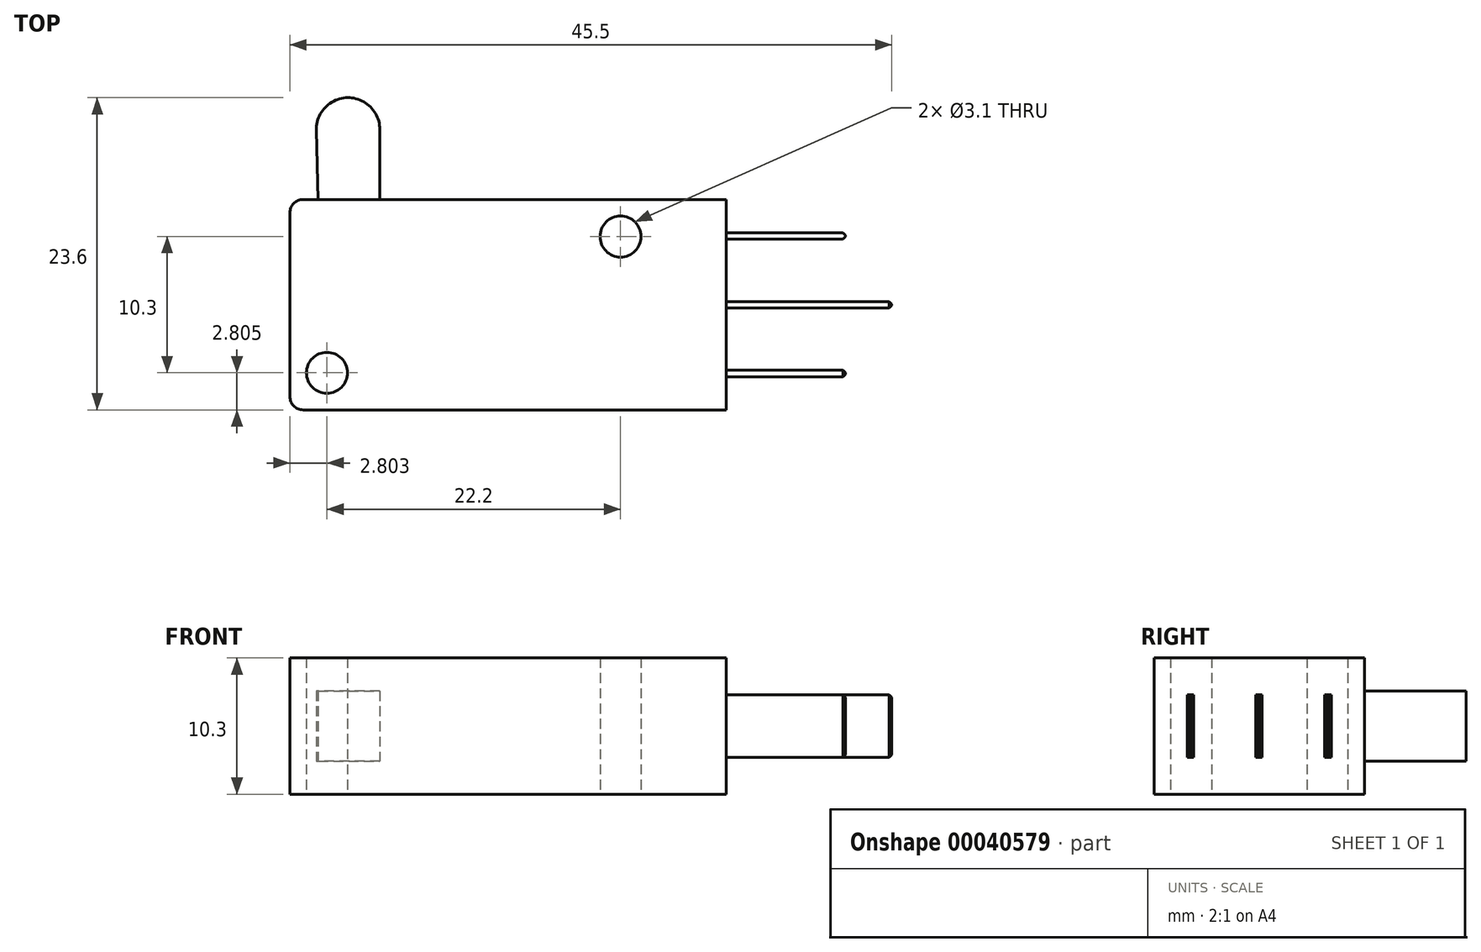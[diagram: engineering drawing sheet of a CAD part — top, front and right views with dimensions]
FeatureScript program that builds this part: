
annotation { "Feature Type Name" : "Feature", "Feature Type Description" : "" }
export const myFeature = defineFeature(function(context is Context, id is Id, definition is map)
    precondition{}
    {
        {
            var Q0;
            Q0=qCreatedBy(makeId("Top.planeOp"),FACE);
            var sketch = newSketch(context, id + "F0", { "sketchPlane" : qUnion([Q0])});
            skLineSegment(sketch, "E0.bottom", {"start": v(-25.87, -19.74) * mm, "end": v(7.13, -19.74) * mm});
            skLineSegment(sketch, "E0.top", {"start": v(-25.87, -35.64) * mm, "end": v(7.13, -35.64) * mm});
            skLineSegment(sketch, "E0.left", {"start": v(-25.87, -19.74) * mm, "end": v(-25.87, -35.64) * mm});
            skLineSegment(sketch, "E0.right", {"start": v(7.13, -19.74) * mm, "end": v(7.13, -35.64) * mm});
            skPoint(sketch, "E1", {"position": v(-23.07, -32.84) * mm});
            skPoint(sketch, "E2", {"position": v(-0.87, -22.54) * mm});
            skCircle(sketch, "E3", {"center": v(-21.47, -14.44) * mm, "radius": 2.4 * mm});
            skLineSegment(sketch, "E4", {"start": v(-19.07, -14.44) * mm, "end": v(-19.07, -19.74) * mm});
            skLineSegment(sketch, "E5", {"start": v(-23.87, -14.5) * mm, "end": v(-23.73, -19.74) * mm});
            skCircle(sketch, "E6", {"center": v(-0.87, -22.54) * mm, "radius": 1.55 * mm});
            skCircle(sketch, "E7", {"center": v(-23.07, -32.84) * mm, "radius": 1.55 * mm});
            skSolve(sketch);
        }
        {
            var Q0;
            Q0=makeQuery(id+"F0.imprint","IMPRINT",FACE,{"disambiguationData":[TD([[makeQuery(id+"F0.imprint","IMPRINT",EDGE,{"derivedFrom":sQuery(id+"F0.wireOp",EDGE,"E0.top")}),1.0]])]});
            var Q1;
            {var subQ0=sQuery(id+"F0.wireOp",EDGE,"E4");Q1=makeQuery(id+"F0.imprint","IMPRINT",FACE,{"disambiguationData":[TD([[makeQuery(id+"F0.imprint","IMPRINT",EDGE,{"derivedFrom":subQ0}),-1.0]])]});}
            var Q2;
            {var subQ0=sQuery(id+"F0.wireOp",EDGE,"E3");var subQ1=makeQuery(id+"F0.imprint","INTERSECT",VERTEX,{"derivedFrom":[subQ0,sQuery(id+"F0.wireOp",EDGE,"E4")]});Q2=makeQuery(id+"F0.imprint","IMPRINT",FACE,{"disambiguationData":[TD([[makeQuery(id+"F0.imprint","IMPRINT",EDGE,{"disambiguationData":[TD([[subQ1,-1.0]])],"derivedFrom":subQ0}),1.0]])]});}
            extrude(context, id + "F1", {"entities" : qUnion([Q0, Q1, Q2]), "depth" : 10.3 * mm});
        }
        {
            var Q0;
            Q0=makeQuery(id+"F1.opExtrude","CAP_FACE",FACE,{"disambiguationData":[OSD([sQuery(id+"F0.wireOp",EDGE,"E0.bottom"),sQuery(id+"F0.wireOp",EDGE,"E0.top"),sQuery(id+"F0.wireOp",EDGE,"E0.left"),sQuery(id+"F0.wireOp",EDGE,"E0.right"),sQuery(id+"F0.wireOp",EDGE,"E3"),sQuery(id+"F0.wireOp",EDGE,"E4"),sQuery(id+"F0.wireOp",EDGE,"E5"),sQuery(id+"F0.wireOp",EDGE,"E6"),sQuery(id+"F0.wireOp",EDGE,"E7")])],"isStart":false});
            var sketch = newSketch(context, id + "F2", { "sketchPlane" : qUnion([Q0])});
            skLineSegment(sketch, "E8", {"start": v(-23.73, -19.74) * mm, "end": v(-19.07, -19.74) * mm});
            skSolve(sketch);
        }
        {
            var Q0;
            Q0=makeQuery(id+"F2.imprint","IMPRINT",FACE,{"disambiguationData":[TD([[makeQuery(id+"F2.imprint","IMPRINT",EDGE,{"derivedFrom":sQuery(id+"F2.wireOp",EDGE,"E8")}),1.0]])]});
            extrude(context, id + "F3", {"entities" : qUnion([Q0]), "operationType" : NewBodyOperationType.REMOVE, "oppositeDirection" : true, "depth" : 2.5 * mm});
        }
        {
            var Q0;
            {var subQ0=sQuery(id+"F0.wireOp",EDGE,"E4");Q0=makeQuery(id+"F0.imprint","IMPRINT",FACE,{"disambiguationData":[TD([[makeQuery(id+"F0.imprint","IMPRINT",EDGE,{"derivedFrom":subQ0}),-1.0]])]});}
            var Q1;
            {var subQ0=sQuery(id+"F0.wireOp",EDGE,"E3");var subQ1=makeQuery(id+"F0.imprint","INTERSECT",VERTEX,{"derivedFrom":[subQ0,sQuery(id+"F0.wireOp",EDGE,"E4")]});Q1=makeQuery(id+"F0.imprint","IMPRINT",FACE,{"disambiguationData":[TD([[makeQuery(id+"F0.imprint","IMPRINT",EDGE,{"disambiguationData":[TD([[subQ1,-1.0]])],"derivedFrom":subQ0}),1.0]])]});}
            extrude(context, id + "F4", {"entities" : qUnion([Q0, Q1]), "operationType" : NewBodyOperationType.REMOVE, "depth" : 2.5 * mm});
        }
        {
            var Q0;
            Q0=makeQuery(id+"F1.opExtrude","SWEPT_FACE",FACE,{"disambiguationData":[OSD([sQuery(id+"F0.wireOp",EDGE,"E0.right")])]});
            var sketch = newSketch(context, id + "F5", { "sketchPlane" : qUnion([Q0])});
            skLineSegment(sketch, "E9", {"start": v(-22.24, 10.3) * mm, "end": v(-22.24, 0) * mm, "construction": true});
            skLineSegment(sketch, "E10", {"start": v(-22.74, 10.3) * mm, "end": v(-22.74, 0) * mm, "construction": true});
            skLineSegment(sketch, "E11", {"start": v(-27.44, 10.3) * mm, "end": v(-27.44, 0) * mm, "construction": true});
            skLineSegment(sketch, "E12", {"start": v(-27.94, 10.3) * mm, "end": v(-27.94, 0) * mm, "construction": true});
            skLineSegment(sketch, "E13", {"start": v(-32.64, 10.3) * mm, "end": v(-32.64, 0) * mm, "construction": true});
            skLineSegment(sketch, "E14", {"start": v(-33.14, 10.3) * mm, "end": v(-33.14, 0) * mm, "construction": true});
            skLineSegment(sketch, "E15", {"start": v(-19.74, 5.15) * mm, "end": v(-35.64, 5.15) * mm, "construction": true});
            skLineSegment(sketch, "E16", {"start": v(-19.74, 7.53) * mm, "end": v(-35.64, 7.53) * mm, "construction": true});
            skLineSegment(sketch, "E17.MirrorCS", {"start": v(-19.74, 2.78) * mm, "end": v(-35.64, 2.78) * mm, "construction": true});
            skPoint(sketch, "E18.oppositeSnap0", {"position": v(-22.74, 5.15) * mm});
            skLineSegment(sketch, "E18.bottom", {"start": v(-22.24, 7.53) * mm, "end": v(-22.74, 7.53) * mm});
            skLineSegment(sketch, "E18.top", {"start": v(-22.24, 2.78) * mm, "end": v(-22.74, 2.78) * mm});
            skLineSegment(sketch, "E18.left", {"start": v(-22.24, 7.53) * mm, "end": v(-22.24, 2.78) * mm});
            skLineSegment(sketch, "E18.right", {"start": v(-22.74, 7.53) * mm, "end": v(-22.74, 2.78) * mm});
            skPoint(sketch, "E19.oppositeSnap0", {"position": v(-27.94, 5.15) * mm});
            skLineSegment(sketch, "E19.bottom", {"start": v(-27.46, 7.53) * mm, "end": v(-27.94, 7.53) * mm});
            skLineSegment(sketch, "E19.top", {"start": v(-27.46, 2.78) * mm, "end": v(-27.94, 2.78) * mm});
            skLineSegment(sketch, "E19.left", {"start": v(-27.46, 7.53) * mm, "end": v(-27.46, 2.78) * mm});
            skLineSegment(sketch, "E19.right", {"start": v(-27.94, 7.53) * mm, "end": v(-27.94, 2.78) * mm});
            skLineSegment(sketch, "E20.bottom", {"start": v(-32.64, 7.53) * mm, "end": v(-33.14, 7.53) * mm});
            skLineSegment(sketch, "E20.top", {"start": v(-32.64, 2.78) * mm, "end": v(-33.14, 2.78) * mm});
            skLineSegment(sketch, "E20.left", {"start": v(-32.64, 7.53) * mm, "end": v(-32.64, 2.78) * mm});
            skLineSegment(sketch, "E20.right", {"start": v(-33.14, 7.53) * mm, "end": v(-33.14, 2.78) * mm});
            skSolve(sketch);
        }
        {
            var Q0;
            Q0=makeQuery(id+"F5.imprint","IMPRINT",FACE,{"disambiguationData":[TD([[makeQuery(id+"F5.imprint","IMPRINT",EDGE,{"derivedFrom":sQuery(id+"F5.wireOp",EDGE,"E18.bottom")}),1.0]])]});
            var Q1;
            Q1=makeQuery(id+"F5.imprint","IMPRINT",FACE,{"disambiguationData":[TD([[makeQuery(id+"F5.imprint","IMPRINT",EDGE,{"derivedFrom":sQuery(id+"F5.wireOp",EDGE,"E20.bottom")}),1.0]])]});
            extrude(context, id + "F6", {"entities" : qUnion([Q0, Q1]), "operationType" : NewBodyOperationType.ADD, "depth" : 9 * mm});
        }
        {
            var Q0;
            Q0=makeQuery(id+"F5.imprint","IMPRINT",FACE,{"disambiguationData":[TD([[makeQuery(id+"F5.imprint","IMPRINT",EDGE,{"derivedFrom":sQuery(id+"F5.wireOp",EDGE,"E19.bottom")}),1.0]])]});
            extrude(context, id + "F7", {"entities" : qUnion([Q0]), "operationType" : NewBodyOperationType.ADD, "depth" : 12.5 * mm});
        }
        {
            var Q0;
            Q0=makeQuery(id+"F6.opExtrude","CAP_EDGE",EDGE,{"disambiguationData":[OSD([sQuery(id+"F5.wireOp",EDGE,"E18.left")])],"isStart":false});
            var Q1;
            Q1=makeQuery(id+"F6.opExtrude","CAP_EDGE",EDGE,{"disambiguationData":[OSD([sQuery(id+"F5.wireOp",EDGE,"E18.right")])],"isStart":false});
            var Q2;
            Q2=makeQuery(id+"F7.opExtrude","CAP_FACE",FACE,{"disambiguationData":[OSD([sQuery(id+"F5.wireOp",EDGE,"E19.bottom"),sQuery(id+"F5.wireOp",EDGE,"E19.top"),sQuery(id+"F5.wireOp",EDGE,"E19.left"),sQuery(id+"F5.wireOp",EDGE,"E19.right")])],"isStart":false});
            var Q3;
            Q3=makeQuery(id+"F6.opExtrude","CAP_FACE",FACE,{"disambiguationData":[OSD([sQuery(id+"F5.wireOp",EDGE,"E20.bottom"),sQuery(id+"F5.wireOp",EDGE,"E20.top"),sQuery(id+"F5.wireOp",EDGE,"E20.left"),sQuery(id+"F5.wireOp",EDGE,"E20.right")])],"isStart":false});
            chamfer(context, id + "F8", {"entities" : qUnion([Q0, Q1, Q2, Q3]), "width" : .2 * mm, "tangentPropagation" : true});
        }
        {
            var Q0;
            Q0=makeQuery(id+"F1.opExtrude","SWEPT_EDGE",EDGE,{"disambiguationData":[OSD([sQuery(id+"F0.wireOp",EDGE,"E0.bottom"),sQuery(id+"F0.wireOp",EDGE,"E0.left")])]});
            var Q1;
            Q1=makeQuery(id+"F1.opExtrude","SWEPT_EDGE",EDGE,{"disambiguationData":[OSD([sQuery(id+"F0.wireOp",EDGE,"E0.top"),sQuery(id+"F0.wireOp",EDGE,"E0.left")])]});
            fillet(context, id + "F9", {"entities" : qUnion([Q0, Q1]), "radius" : 1 * mm, "tangentPropagation" : true, "allowEdgeOverflow" : false});
        }
    });
